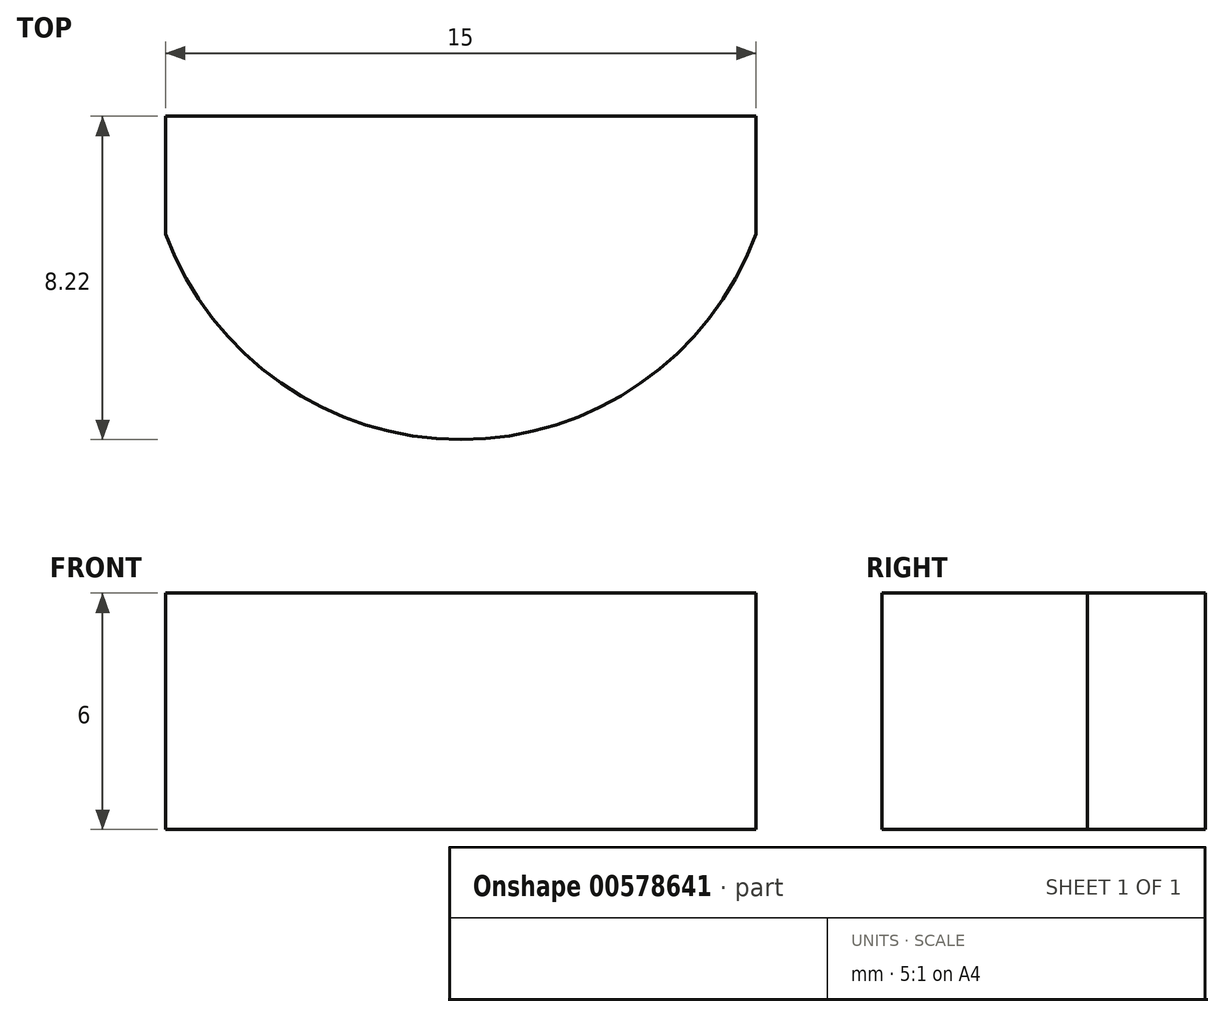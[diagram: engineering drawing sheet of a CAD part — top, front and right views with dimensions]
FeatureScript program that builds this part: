
annotation { "Feature Type Name" : "Feature", "Feature Type Description" : "" }
export const myFeature = defineFeature(function(context is Context, id is Id, definition is map)
    precondition{}
    {
        {
            var Q0;
            Q0=qCreatedBy(makeId("Top.planeOp"),FACE);
            var sketch = newSketch(context, id + "F0", { "sketchPlane" : qUnion([Q0])});
            skLineSegment(sketch, "E0", {"start": v(-7.94, 0) * mm, "end": v(7.06, 0) * mm});
            skLineSegment(sketch, "E1", {"start": v(-7.94, 0) * mm, "end": v(-7.94, -3) * mm});
            skLineSegment(sketch, "E2", {"start": v(-7.94, -3) * mm, "end": v(7.06, -3) * mm});
            skLineSegment(sketch, "E3", {"start": v(7.06, -3) * mm, "end": v(7.06, 0) * mm});
            skArc(sketch, "E4", {"start": v(-7.94, -3) * mm, "mid": v(-0.44, -8.22) * mm, "end": v(7.06, -3) * mm});
            skSolve(sketch);
        }
        {
            var Q0;
            Q0 = qSketchRegion(id + "F0", true);
            extrude(context, id + "F1", {"entities" : qUnion([Q0]), "depth" : 6 * mm, "offsetDistance" : 25 * mm});
        }
    });
